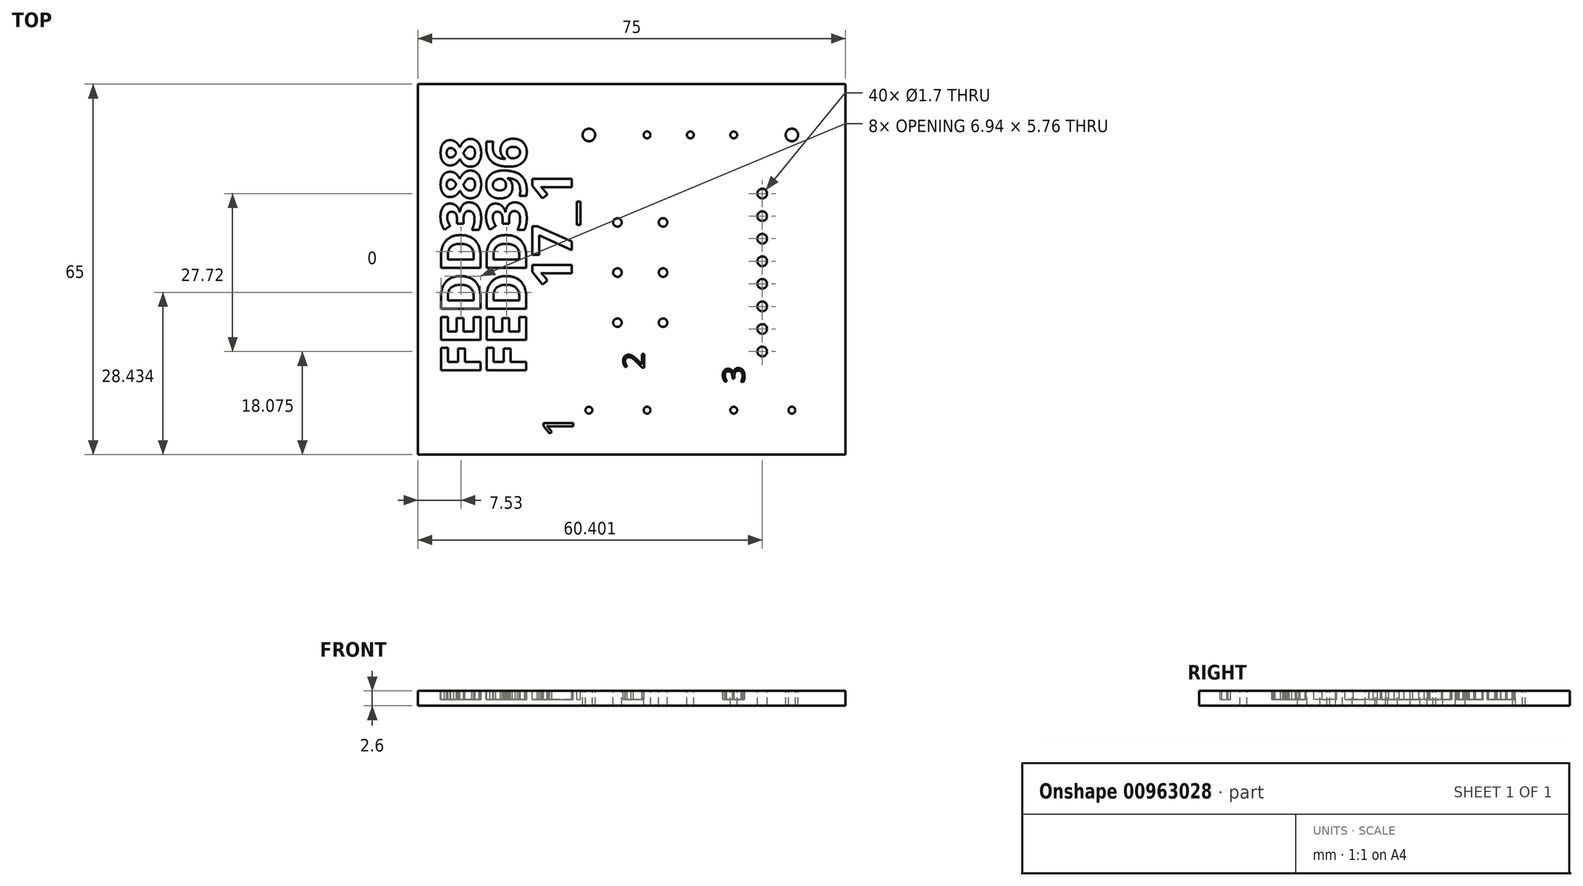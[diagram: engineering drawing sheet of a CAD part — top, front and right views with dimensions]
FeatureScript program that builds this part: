
annotation { "Feature Type Name" : "Feature", "Feature Type Description" : "" }
export const myFeature = defineFeature(function(context is Context, id is Id, definition is map)
    precondition{}
    {
        {
            var Q0;
            Q0=qCreatedBy(makeId("Top.planeOp"),FACE);
            var sketch = newSketch(context, id + "F0", { "sketchPlane" : qUnion([Q0])});
            skLineSegment(sketch, "E0.bottom", {"start": v(-43.16, 43.34) * mm, "end": v(31.84, 43.34) * mm});
            skLineSegment(sketch, "E0.top", {"start": v(-43.16, -21.66) * mm, "end": v(31.84, -21.66) * mm});
            skLineSegment(sketch, "E0.left", {"start": v(-43.16, 43.34) * mm, "end": v(-43.16, -21.66) * mm});
            skLineSegment(sketch, "E0.right", {"start": v(31.84, 43.34) * mm, "end": v(31.84, -21.66) * mm});
            skSolve(sketch);
        }
        {
            var Q0;
            Q0=makeQuery(id+"F0.imprint","IMPRINT",FACE,{"disambiguationData":[TD([[makeQuery(id+"F0.imprint","IMPRINT",EDGE,{"derivedFrom":sQuery(id+"F0.wireOp",EDGE,"E0.bottom")}),-1.0]])]});
            extrude(context, id + "F1", {"entities" : qUnion([Q0]), "depth" : 2.6 * mm, "offsetDistance" : 25 * mm});
        }
        {
            var Q0;
            Q0=makeQuery(id+"F1.opExtrude","CAP_FACE",FACE,{"disambiguationData":[OSD([sQuery(id+"F0.wireOp",EDGE,"E0.bottom"),sQuery(id+"F0.wireOp",EDGE,"E0.top"),sQuery(id+"F0.wireOp",EDGE,"E0.left"),sQuery(id+"F0.wireOp",EDGE,"E0.right")])],"isStart":false});
            var sketch = newSketch(context, id + "F2", { "sketchPlane" : qUnion([Q0])});
            skText(sketch, "E1", { "text": "FEDD388\n", "fontName": "OpenSans-Bold.ttf"});
            skText(sketch, "E2", { "text": "1", "fontName": "OpenSans-Regular.ttf"});
            skText(sketch, "E3", { "text": "2", "fontName": "OpenSans-Regular.ttf"});
            skText(sketch, "E4", { "text": "3", "fontName": "OpenSans-Regular.ttf"});
            skText(sketch, "E5", { "text": "FEDD396", "fontName": "OpenSans-Bold.ttf"});
            skText(sketch, "E6", { "text": "17_1", "fontName": "OpenSans-Bold.ttf"});
            const initialGuessF2  = {"E1": [-0.03216, -0.00776, 0, 1, 0.007], "E2": [-0.01594, -0.01866, 0, 1, 0.00522], "E3": [-0.00345, -0.00666, 0, 1, 0.0037], "E4": [0.01409, -0.00916, 0, 1, 0.00374], "E5": [-0.02416, -0.00776, 0, 1, 0.007], "E6": [-0.01616, 0.0076, 0, 1, 0.007]};
            skSetInitialGuess(sketch, initialGuessF2);
            skSolve(sketch);
        }
        {
            var Q0;
            Q0=qSketchRegion(id+"F2",true);
            extrude(context, id + "F3", {"entities" : qUnion([Q0]), "operationType" : NewBodyOperationType.REMOVE, "oppositeDirection" : true, "depth" : 1.5 * mm, "offsetDistance" : 25 * mm});
        }
        {
            var Q0;
            {var subQ0=sQuery(id+"F0.wireOp",EDGE,"E0.left");var subQ1=sQuery(id+"F0.wireOp",EDGE,"E0.bottom");var subQ2=sQuery(id+"F0.wireOp",EDGE,"E0.right");var subQ3=sQuery(id+"F0.wireOp",EDGE,"E0.top");Q0=makeQuery(id+"F3.boolean.opBoolean","SPLIT",FACE,{"disambiguationData":[TD([makeQuery(id+"F1.opExtrude","SWEPT_FACE",FACE,{"disambiguationData":[OSD([subQ1])]})])],"derivedFrom":makeQuery(id+"F1.opExtrude","CAP_FACE",FACE,{"disambiguationData":[OSD([subQ1,subQ3,subQ0,subQ2])],"isStart":false})});}
            var sketch = newSketch(context, id + "F4", { "sketchPlane" : qUnion([Q0])});
            skCircle(sketch, "E7", {"center": v(17.24, -3.58) * mm, "radius": 0.85 * mm});
            skCircle(sketch, "E8", {"center": v(17.24, 0.38) * mm, "radius": 0.85 * mm});
            skCircle(sketch, "E9", {"center": v(17.24, 4.34) * mm, "radius": 0.85 * mm});
            skCircle(sketch, "E10", {"center": v(17.24, 8.3) * mm, "radius": 0.85 * mm});
            skCircle(sketch, "E11", {"center": v(17.24, 12.26) * mm, "radius": 0.85 * mm});
            skCircle(sketch, "E12", {"center": v(17.24, 16.22) * mm, "radius": 0.85 * mm});
            skCircle(sketch, "E13", {"center": v(17.24, 20.18) * mm, "radius": 0.85 * mm});
            skCircle(sketch, "E14", {"center": v(17.24, 24.14) * mm, "radius": 0.85 * mm});
            skCircle(sketch, "E15", {"center": v(-8.16, 1.48) * mm, "radius": 0.75 * mm});
            skCircle(sketch, "E16", {"center": v(-8.16, 10.28) * mm, "radius": 0.75 * mm});
            skCircle(sketch, "E17", {"center": v(-8.16, 19.08) * mm, "radius": 0.75 * mm});
            skCircle(sketch, "E18", {"center": v(-0.16, 1.48) * mm, "radius": 0.75 * mm});
            skCircle(sketch, "E19", {"center": v(-0.16, 10.28) * mm, "radius": 0.75 * mm});
            skCircle(sketch, "E20", {"center": v(-0.16, 19.08) * mm, "radius": 0.75 * mm});
            skCircle(sketch, "E21", {"center": v(-13.16, -13.87) * mm, "radius": 0.6 * mm});
            skCircle(sketch, "E22", {"center": v(-13.16, 34.43) * mm, "radius": 1.1 * mm});
            skCircle(sketch, "E23", {"center": v(22.44, 34.43) * mm, "radius": 1.1 * mm});
            skCircle(sketch, "E24", {"center": v(22.44, -13.87) * mm, "radius": 0.6 * mm});
            skCircle(sketch, "E25", {"center": v(-2.96, 34.43) * mm, "radius": 0.6 * mm});
            skCircle(sketch, "E26", {"center": v(4.64, 34.43) * mm, "radius": 0.6 * mm});
            skCircle(sketch, "E27", {"center": v(12.24, 34.43) * mm, "radius": 0.6 * mm});
            skCircle(sketch, "E28", {"center": v(-2.96, -13.87) * mm, "radius": 0.6 * mm});
            skCircle(sketch, "E29", {"center": v(12.24, -13.87) * mm, "radius": 0.6 * mm});
            skSolve(sketch);
        }
        {
            var Q0;
            Q0 = qSketchRegion(id + "F4", true);
            extrude(context, id + "F5", {"entities" : qUnion([Q0]), "operationType" : NewBodyOperationType.REMOVE, "endBound" : BoundingType.UP_TO_NEXT, "oppositeDirection" : true, "depth" : 25 * mm, "offsetDistance" : 25 * mm});
        }
    });
